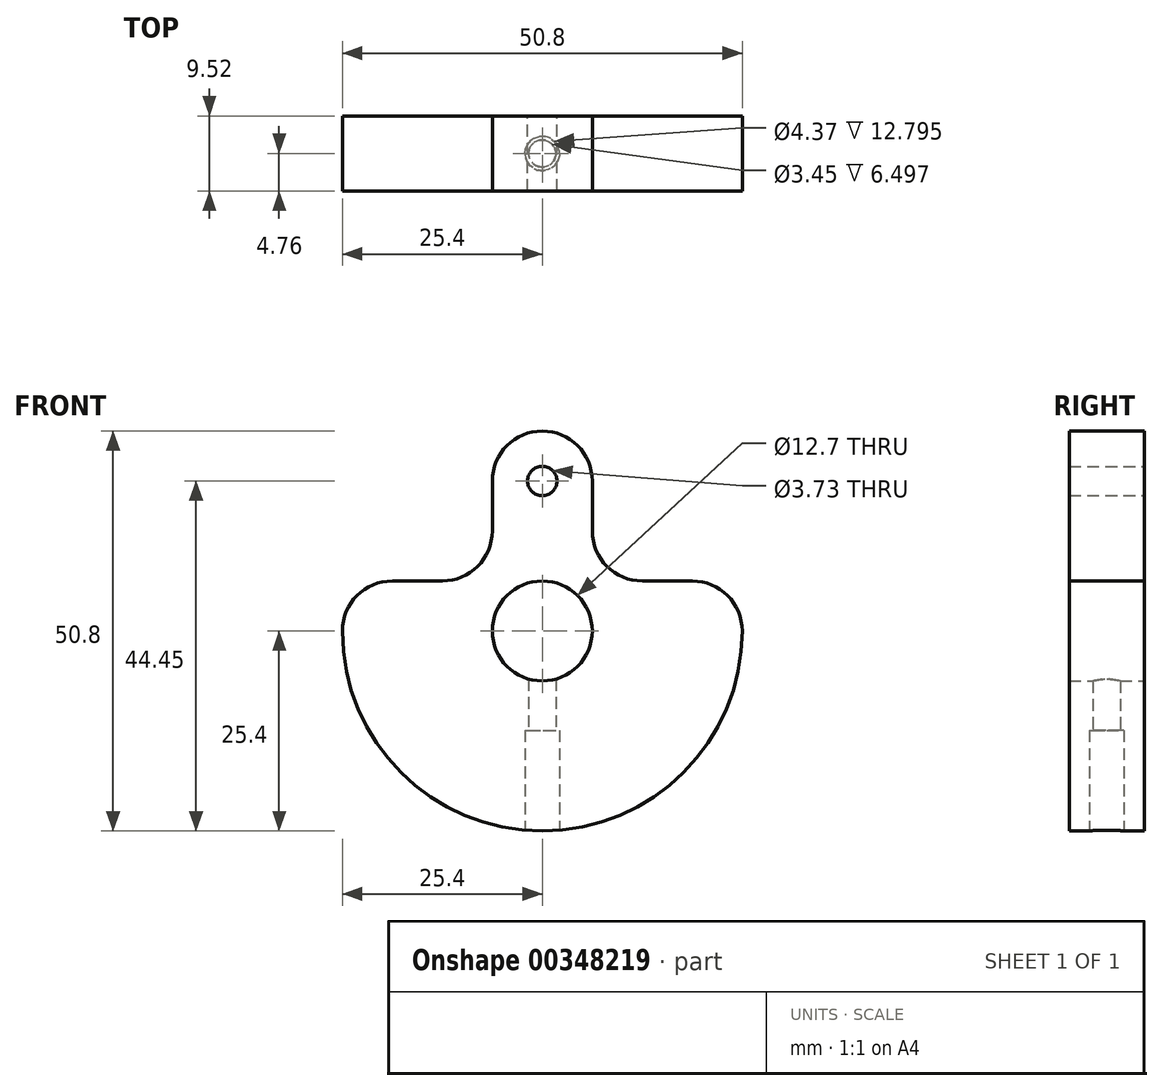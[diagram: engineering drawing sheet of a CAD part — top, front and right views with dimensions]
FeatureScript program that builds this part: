
annotation { "Feature Type Name" : "Feature", "Feature Type Description" : "" }
export const myFeature = defineFeature(function(context is Context, id is Id, definition is map)
    precondition{}
    {
        {
            var Q0;
            Q0=qCreatedBy(makeId("Front.planeOp"),FACE);
            var sketch = newSketch(context, id + "F0", { "sketchPlane" : qUnion([Q0])});
            skArc(sketch, "E0", {"start": v(25.4, 0) * mm, "mid": v(0, -25.4) * mm, "end": v(-25.4, 0) * mm});
            skCircle(sketch, "E1", {"center": v(0, 0) * mm, "radius": 6.35 * mm});
            skCircle(sketch, "E2", {"center": v(0, 19.05) * mm, "radius": 1.87 * mm});
            skArc(sketch, "E3", {"start": v(-6.35, 19.05) * mm, "mid": v(0, 25.4) * mm, "end": v(6.35, 19.05) * mm});
            skLineSegment(sketch, "E4", {"start": v(-6.35, 19.05) * mm, "end": v(-6.35, 12.7) * mm});
            skLineSegment(sketch, "E5", {"start": v(6.35, 19.05) * mm, "end": v(6.35, 12.7) * mm});
            skLineSegment(sketch, "E6", {"start": v(-12.7, 6.35) * mm, "end": v(-19.05, 6.35) * mm});
            skLineSegment(sketch, "E7", {"start": v(12.7, 6.35) * mm, "end": v(19.05, 6.35) * mm});
            skArc(sketch, "E8", {"start": v(25.4, 0) * mm, "mid": v(23.54, 4.5) * mm, "end": v(19.05, 6.35) * mm});
            skArc(sketch, "E9", {"start": v(-25.4, 0) * mm, "mid": v(-23.54, 4.5) * mm, "end": v(-19.05, 6.35) * mm});
            skArc(sketch, "E10", {"start": v(-6.35, 12.7) * mm, "mid": v(-8.2, 8.2) * mm, "end": v(-12.7, 6.35) * mm});
            skArc(sketch, "E11", {"start": v(6.35, 12.7) * mm, "mid": v(8.2, 8.2) * mm, "end": v(12.7, 6.35) * mm});
            skPoint(sketch, "E12.orphan", {"position": v(-6.35, 6.35) * mm});
            skPoint(sketch, "E13.orphan", {"position": v(6.35, 6.35) * mm});
            skSolve(sketch);
        }
        {
            var Q0;
            Q0=qSketchRegion(id+"F0",true);
            extrude(context, id + "F1", {"entities" : qUnion([Q0]), "endBound" : BoundingType.SYMMETRIC, "depth" : 9.52 * mm});
        }
        {
            var Q0;
            Q0=qCreatedBy(makeId("Top.planeOp"),FACE);
            cPlane(context, id + "F2", {"entities" : qUnion([Q0]), "cplaneType" : CPlaneType.OFFSET, "offset" : 25.4 * mm, "oppositeDirection" : true, "width" : 152.4 * mm, "height" : 152.4 * mm});
        }
        {
            var Q0;
            Q0=qCreatedBy(id+"F2.planeOp",FACE);
            var sketch = newSketch(context, id + "F3", { "sketchPlane" : qUnion([Q0])});
            skPoint(sketch, "E14", {"position": v(0, 0) * mm});
            skSolve(sketch);
        }
        {
            var Q0;
            Q0=sQuery(id+"F3.wireOp",VERTEX,"E14");
            var Q1;
            Q1=makeQuery(id+"F1.opExtrude","SWEPT_BODY",BODY,{"disambiguationData":[OSD([sQuery(id+"F0.wireOp",EDGE,"E0"),sQuery(id+"F0.wireOp",EDGE,"E1"),sQuery(id+"F0.wireOp",EDGE,"E2"),sQuery(id+"F0.wireOp",EDGE,"E3"),sQuery(id+"F0.wireOp",EDGE,"E4"),sQuery(id+"F0.wireOp",EDGE,"E5"),sQuery(id+"F0.wireOp",EDGE,"E6"),sQuery(id+"F0.wireOp",EDGE,"E7"),sQuery(id+"F0.wireOp",EDGE,"E8"),sQuery(id+"F0.wireOp",EDGE,"E9"),sQuery(id+"F0.wireOp",EDGE,"E10"),sQuery(id+"F0.wireOp",EDGE,"E11")])]});
            hole(context, id + "F4", {"style" : HoleStyle.C_BORE, "holeDiameter" : 3.45 * mm, "cBoreDiameter" : 4.37 * mm, "cBoreDepth" : 12.7 * mm, "endStyle" : HoleEndStyle.BLIND, "oppositeDirection" : true, "holeDepth" : 25.4 * mm, "locations" : qUnion([Q0]), "scope" : qUnion([Q1])});
        }
    });
